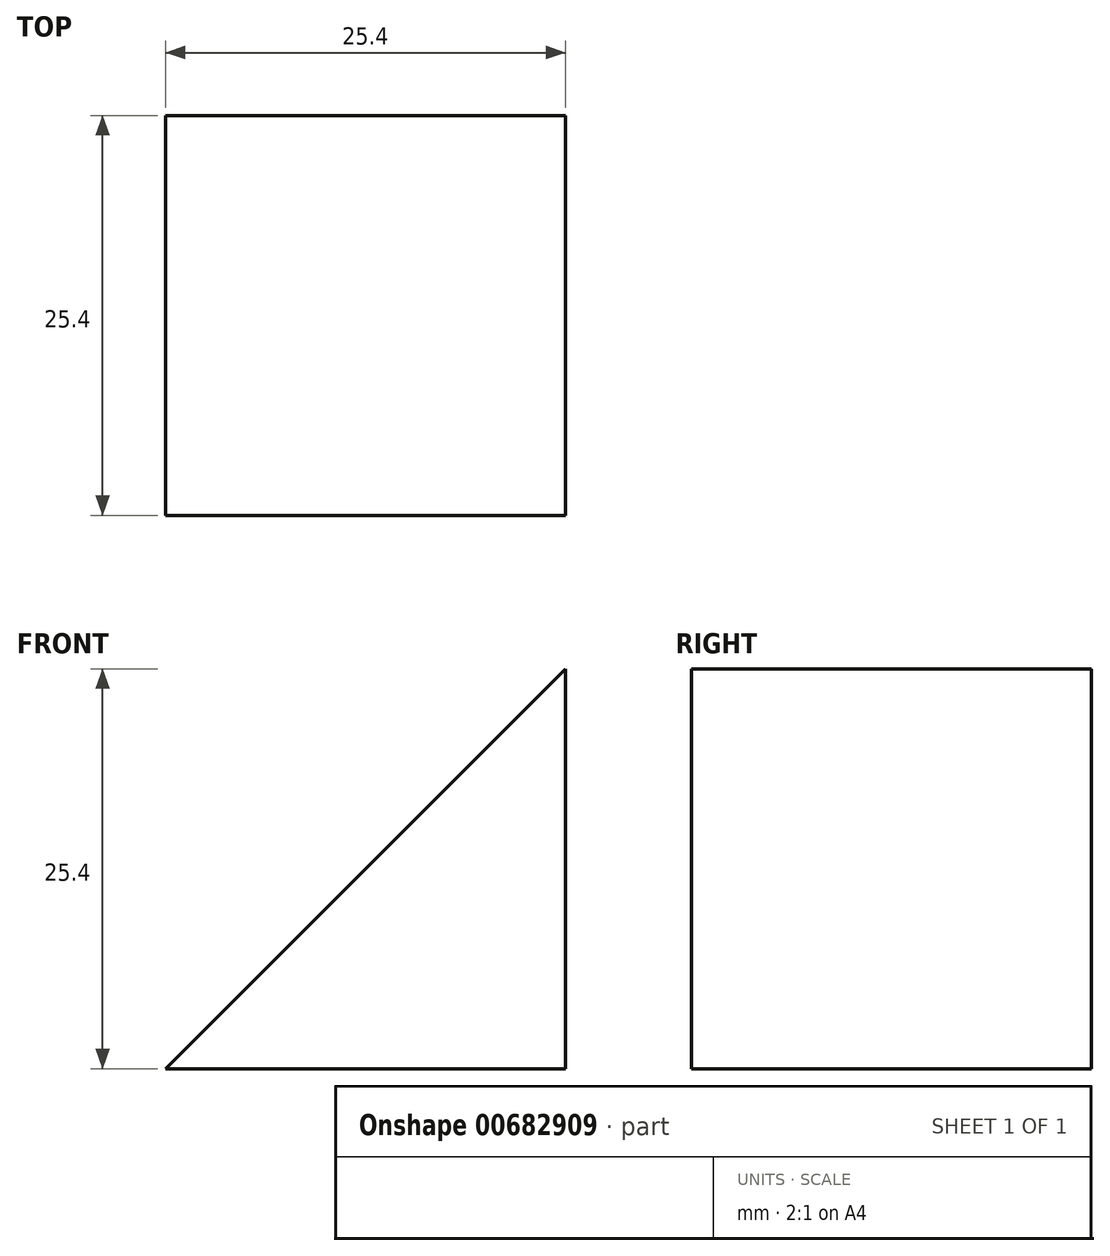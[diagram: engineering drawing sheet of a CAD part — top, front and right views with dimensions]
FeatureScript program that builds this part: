
annotation { "Feature Type Name" : "Feature", "Feature Type Description" : "" }
export const myFeature = defineFeature(function(context is Context, id is Id, definition is map)
    precondition{}
    {
        {
            var Q0;
            Q0=qCreatedBy(makeId("Front.planeOp"),FACE);
            var sketch = newSketch(context, id + "F0", { "sketchPlane" : qUnion([Q0])});
            skLineSegment(sketch, "E0", {"start": v(0, 0) * mm, "end": v(0, 25.4) * mm});
            skLineSegment(sketch, "E1", {"start": v(-25.4, 0) * mm, "end": v(0, 0) * mm});
            skLineSegment(sketch, "E2", {"start": v(-25.4, 0) * mm, "end": v(0, 25.4) * mm});
            skSolve(sketch);
        }
        {
            var Q0;
            Q0=makeQuery(id+"F0.imprint","IMPRINT",FACE,{"disambiguationData":[TD([[makeQuery(id+"F0.imprint","IMPRINT",EDGE,{"derivedFrom":sQuery(id+"F0.wireOp",EDGE,"E0")}),1.0]])]});
            extrude(context, id + "F1", {"entities" : qUnion([Q0]), "depth" : 25.4 * mm, "offsetDistance" : 25.4 * mm});
        }
    });
